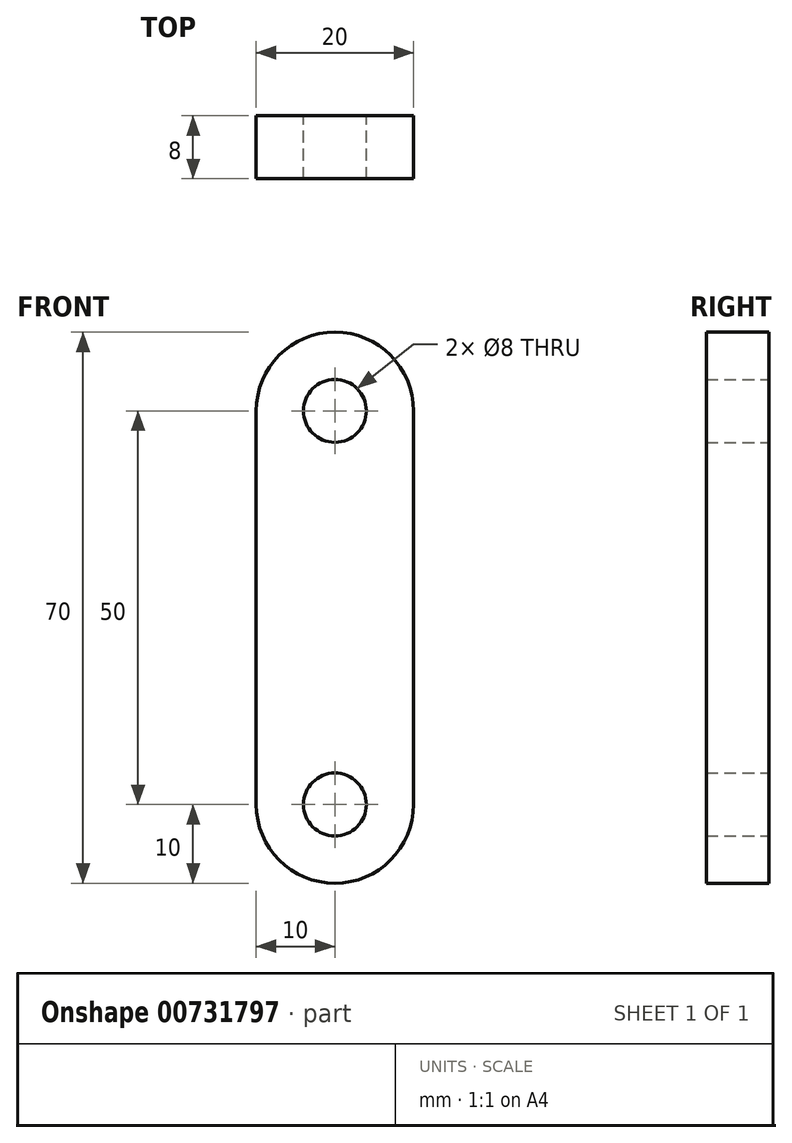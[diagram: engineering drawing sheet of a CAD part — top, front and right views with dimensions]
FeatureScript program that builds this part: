
annotation { "Feature Type Name" : "Feature", "Feature Type Description" : "" }
export const myFeature = defineFeature(function(context is Context, id is Id, definition is map)
    precondition{}
    {
        {
            var Q0;
            Q0=qCreatedBy(makeId("Front.planeOp"),FACE);
            var sketch = newSketch(context, id + "F0", { "sketchPlane" : qUnion([Q0])});
            skCircle(sketch, "E0", {"center": v(0, 0) * mm, "radius": 4 * mm});
            skArc(sketch, "E1", {"start": v(-10, 0) * mm, "mid": v(0, -10) * mm, "end": v(10, 0) * mm});
            skLineSegment(sketch, "E2", {"start": v(-10, 0) * mm, "end": v(-10, 50) * mm});
            skLineSegment(sketch, "E3", {"start": v(10, 0) * mm, "end": v(10, 50) * mm});
            skArc(sketch, "E4", {"start": v(10, 50) * mm, "mid": v(0, 60) * mm, "end": v(-10, 50) * mm});
            skCircle(sketch, "E5", {"center": v(0, 50) * mm, "radius": 4 * mm});
            skSolve(sketch);
        }
        {
            var Q0;
            Q0 = qSketchRegion(id + "F0", true);
            extrude(context, id + "F1", {"entities" : qUnion([Q0]), "depth" : 8 * mm, "offsetDistance" : 25 * mm});
        }
    });
